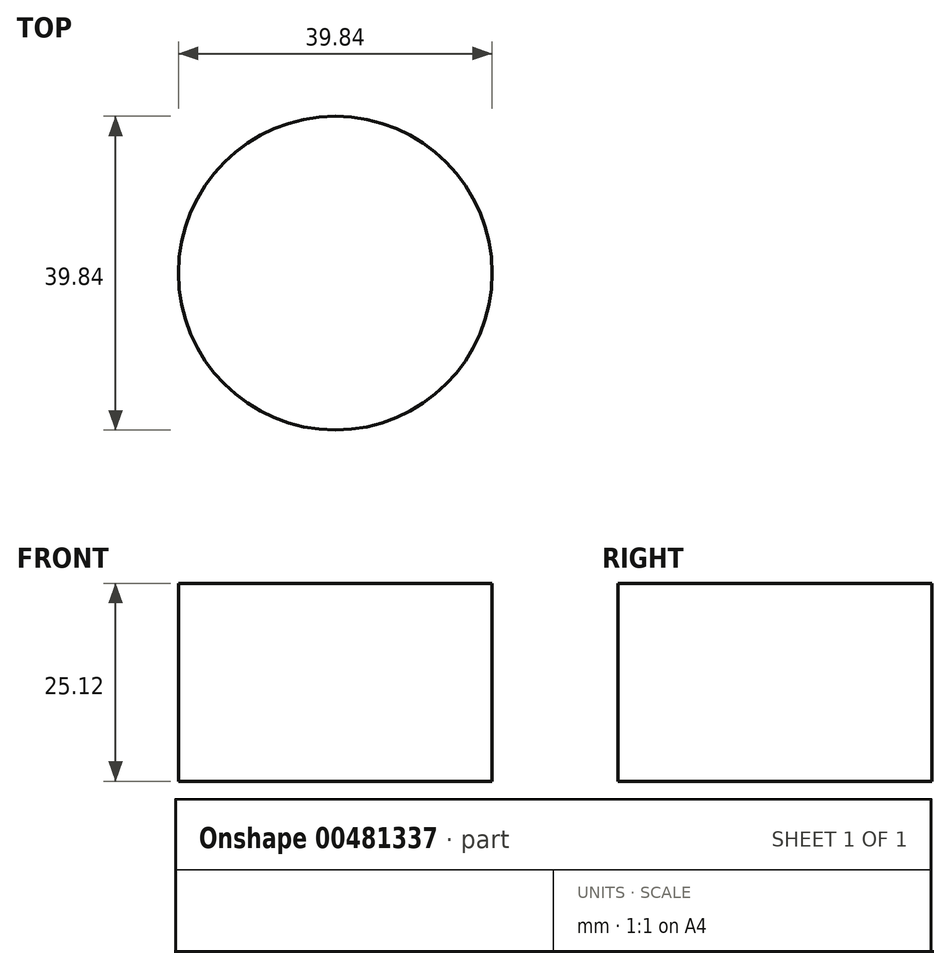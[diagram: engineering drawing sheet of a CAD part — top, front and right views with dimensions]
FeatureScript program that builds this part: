
annotation { "Feature Type Name" : "Feature", "Feature Type Description" : "" }
export const myFeature = defineFeature(function(context is Context, id is Id, definition is map)
    precondition{}
    {
        {
            var Q0;
            Q0=qCreatedBy(makeId("Top.planeOp"),FACE);
            var sketch = newSketch(context, id + "F0", { "sketchPlane" : qUnion([Q0])});
            skCircle(sketch, "E0", {"center": v(24.97, 0) * mm, "radius": 19.92 * mm});
            skSolve(sketch);
        }
        {
            var Q0;
            Q0 = qSketchRegion(id + "F0", true);
            extrude(context, id + "F1", {"entities" : qUnion([Q0]), "depth" : 25.12 * mm});
        }
    });
